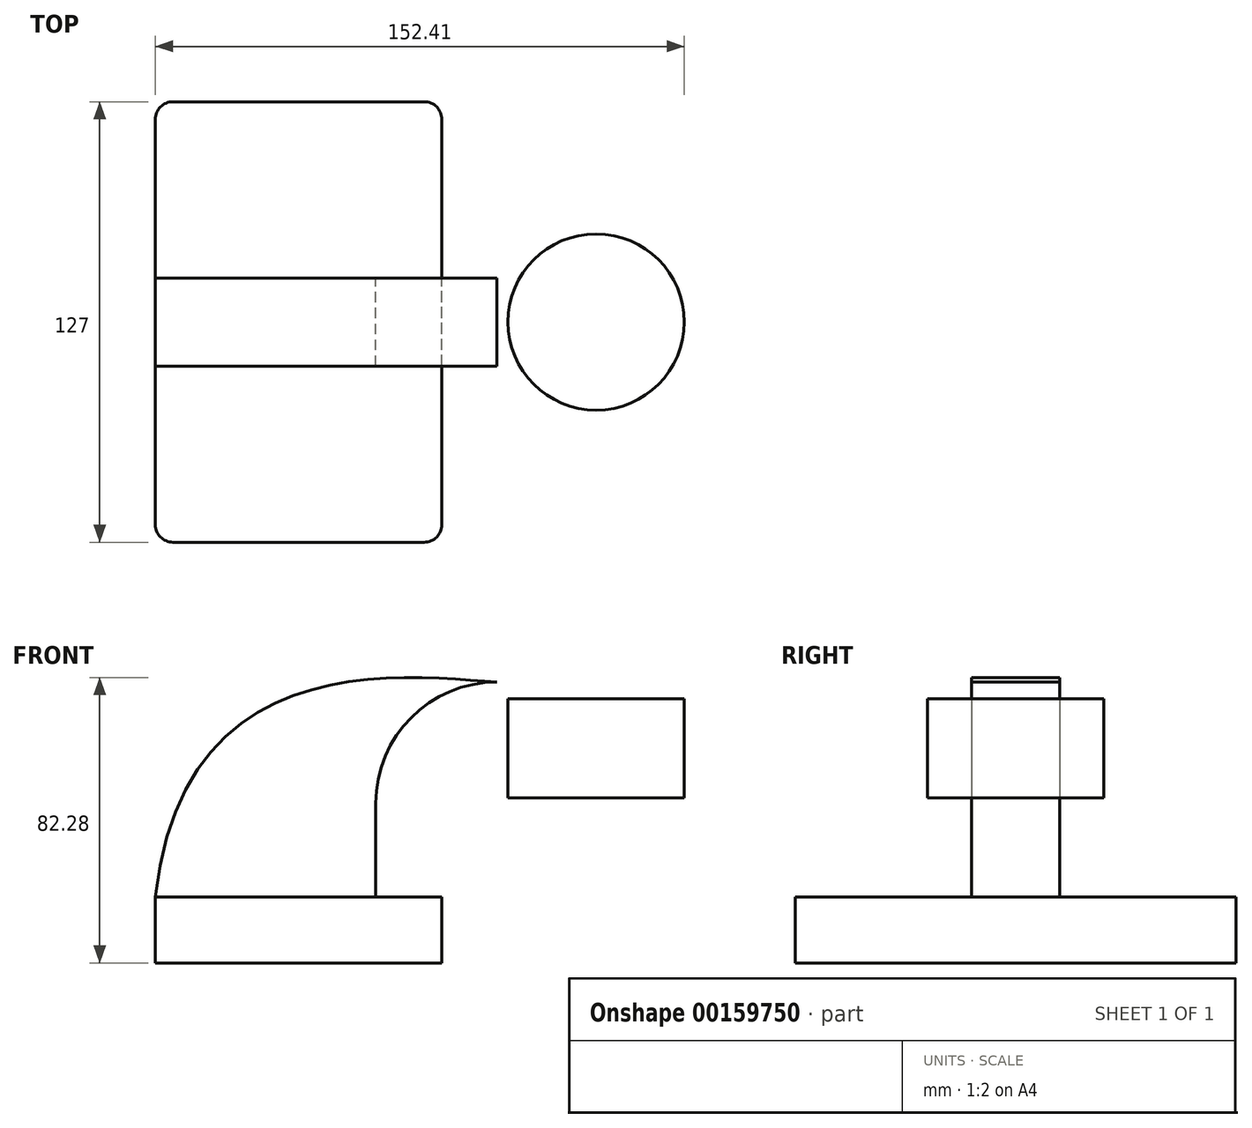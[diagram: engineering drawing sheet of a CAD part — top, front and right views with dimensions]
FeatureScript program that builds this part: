
annotation { "Feature Type Name" : "Feature", "Feature Type Description" : "" }
export const myFeature = defineFeature(function(context is Context, id is Id, definition is map)
    precondition{}
    {
        {
            var Q0;
            Q0=qCreatedBy(makeId("Front.planeOp"),FACE);
            var sketch = newSketch(context, id + "F0", { "sketchPlane" : qUnion([Q0])});
            skLineSegment(sketch, "E0.bottom", {"start": v(-41.28, 9.52) * mm, "end": v(41.28, 9.52) * mm});
            skLineSegment(sketch, "E0.top", {"start": v(-41.28, -9.53) * mm, "end": v(41.28, -9.53) * mm});
            skLineSegment(sketch, "E0.left", {"start": v(-41.28, 9.52) * mm, "end": v(-41.28, -9.53) * mm});
            skLineSegment(sketch, "E0.right", {"start": v(41.28, 9.53) * mm, "end": v(41.28, -9.53) * mm});
            skPoint(sketch, "E0.middle", {"position": v(0, 0) * mm});
            skLineSegment(sketch, "E1.bottom", {"start": v(111.12, 38.1) * mm, "end": v(60.32, 38.1) * mm});
            skLineSegment(sketch, "E1.top", {"start": v(111.12, 66.68) * mm, "end": v(60.32, 66.68) * mm});
            skLineSegment(sketch, "E1.left", {"start": v(111.12, 38.1) * mm, "end": v(111.12, 66.68) * mm});
            skLineSegment(sketch, "E1.right", {"start": v(60.32, 38.1) * mm, "end": v(60.32, 66.68) * mm});
            skPoint(sketch, "E1.middle", {"position": v(85.72, 52.39) * mm});
            skLineSegment(sketch, "E2.bottom", {"start": v(41.27, 36.51) * mm, "end": v(41.27, 36.51) * mm});
            skPoint(sketch, "E2.middle", {"position": v(41.28, 9.53) * mm});
            skArc(sketch, "E3", {"start": v(41.27, 36.51) * mm, "mid": v(45.92, 47.74) * mm, "end": v(57.15, 52.39) * mm});
            skLineSegment(sketch, "E4", {"start": v(57.15, 52.39) * mm, "end": v(85.72, 52.39) * mm});
            skLineSegment(sketch, "E5", {"start": v(41.27, 36.51) * mm, "end": v(41.28, 9.52) * mm});
            skLineSegment(sketch, "E6.0", {"start": v(22.22, 36.51) * mm, "end": v(22.22, 9.52) * mm});
            skArc(sketch, "E6.1", {"start": v(22.22, 36.51) * mm, "mid": v(32.45, 61.2) * mm, "end": v(57.15, 71.44) * mm});
            skLineSegment(sketch, "E6.2", {"start": v(57.15, 71.44) * mm, "end": v(85.72, 71.44) * mm});
            skLineSegment(sketch, "E7", {"start": v(85.72, 38.1) * mm, "end": v(85.72, 71.44) * mm});
            skFitSpline(sketch, "E8", {"points": [v(57.15, 71.44) * mm, v(-41.27, 9.53) * mm], "startDerivative": vector(-78.98, 5.43) * mm, "endDerivative": vector(-23.6, -218.02) * mm});
            skSolve(sketch);
        }
        {
            var Q0;
            Q0=makeQuery(id+"F0.imprint","IMPRINT",FACE,{"disambiguationData":[TD([[makeQuery(id+"F0.imprint","IMPRINT",EDGE,{"derivedFrom":sQuery(id+"F0.wireOp",EDGE,"E0.top")}),1.0]])]});
            extrude(context, id + "F1", {"entities" : qUnion([Q0]), "endBound" : BoundingType.SYMMETRIC, "depth" : 127 * mm});
        }
        {
            var Q0;
            {var subQ2=sQuery(id+"F0.wireOp",EDGE,"E6.0");Q0=makeQuery(id+"F0.imprint","IMPRINT",FACE,{"disambiguationData":[TD([[makeQuery(id+"F0.imprint","IMPRINT",EDGE,{"derivedFrom":subQ2}),-1.0]])]});}
            extrude(context, id + "F2", {"entities" : qUnion([Q0]), "operationType" : NewBodyOperationType.ADD, "endBound" : BoundingType.SYMMETRIC, "depth" : 25.4 * mm});
        }
        {
            var Q0;
            {var subQ0=sQuery(id+"F0.wireOp",EDGE,"E1.left");Q0=makeQuery(id+"F0.imprint","IMPRINT",FACE,{"disambiguationData":[TD([[makeQuery(id+"F0.imprint","IMPRINT",EDGE,{"derivedFrom":subQ0}),1.0]])]});}
            var Q1;
            Q1=sQuery(id+"F0.wireOp",EDGE,"E7");
            revolve(context, id + "F3", {"entities" : qUnion([Q0]), "axis" : qUnion([Q1]), "revolveType" : RevolveType.FULL});
        }
        {
            var Q0;
            Q0=makeQuery(id+"F1.opExtrude","CAP_EDGE",EDGE,{"disambiguationData":[OSD([sQuery(id+"F0.wireOp",EDGE,"E0.right")])],"isStart":true});
            var Q1;
            Q1=makeQuery(id+"F1.opExtrude","CAP_EDGE",EDGE,{"disambiguationData":[OSD([sQuery(id+"F0.wireOp",EDGE,"E0.right")])],"isStart":false});
            var Q2;
            Q2=makeQuery(id+"F1.opExtrude","CAP_EDGE",EDGE,{"disambiguationData":[OSD([sQuery(id+"F0.wireOp",EDGE,"E0.left")])],"isStart":false});
            var Q3;
            Q3=makeQuery(id+"F1.opExtrude","CAP_EDGE",EDGE,{"disambiguationData":[OSD([sQuery(id+"F0.wireOp",EDGE,"E0.left")])],"isStart":true});
            fillet(context, id + "F4", {"entities" : qUnion([Q0, Q1, Q2, Q3]), "radius" : 5.08 * mm, "tangentPropagation" : true, "allowEdgeOverflow" : false});
        }
    });
